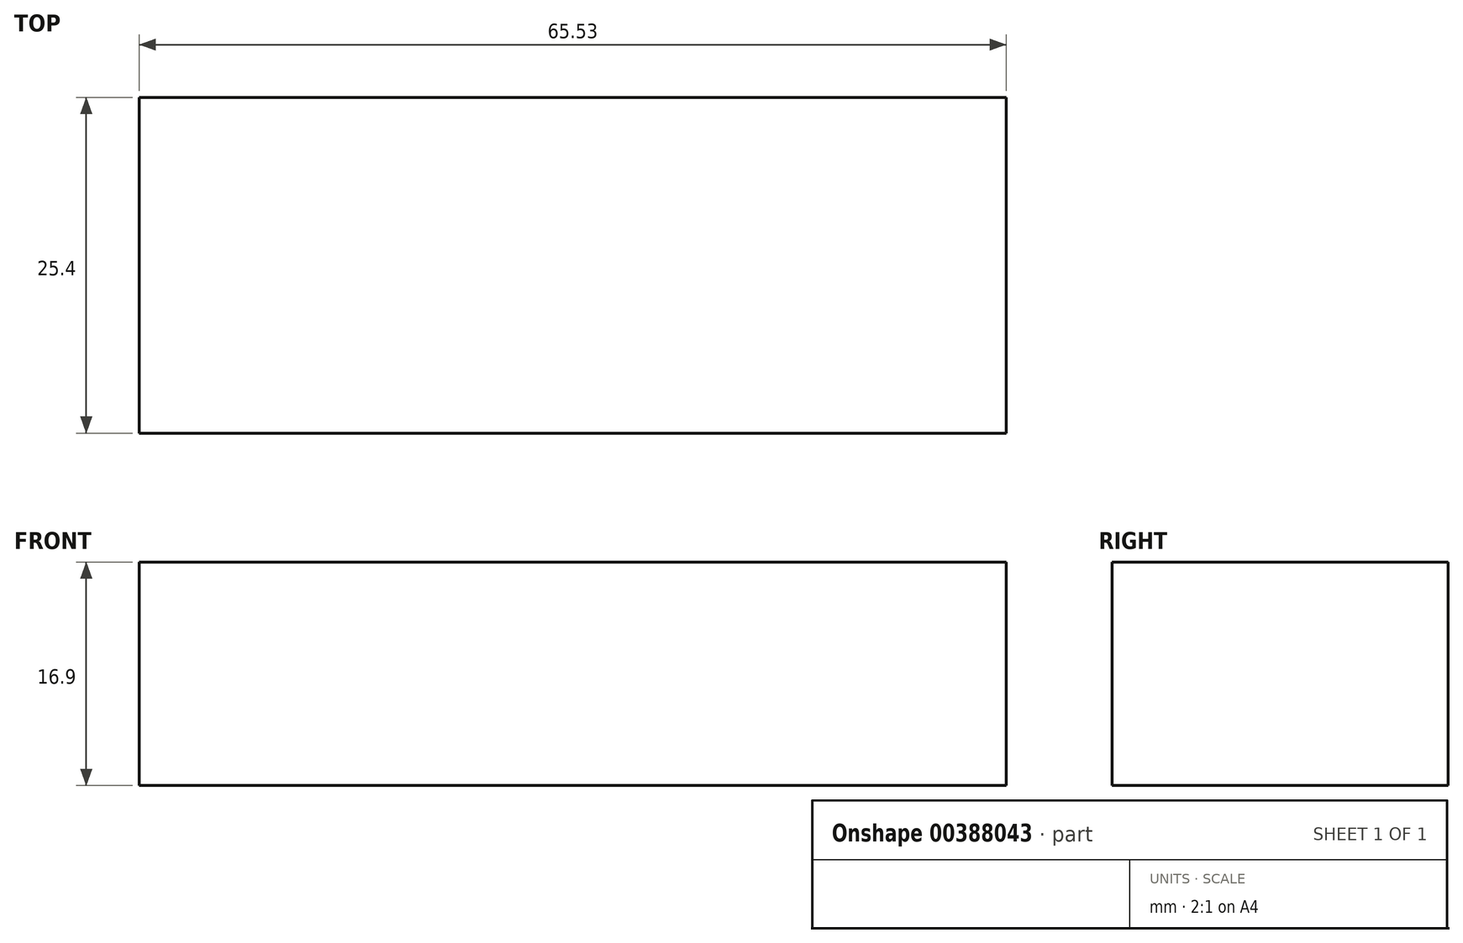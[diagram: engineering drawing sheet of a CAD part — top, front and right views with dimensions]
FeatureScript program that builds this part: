
annotation { "Feature Type Name" : "Feature", "Feature Type Description" : "" }
export const myFeature = defineFeature(function(context is Context, id is Id, definition is map)
    precondition{}
    {
        {
            var Q0;
            Q0=qCreatedBy(makeId("Front.planeOp"),FACE);
            var sketch = newSketch(context, id + "F0", { "sketchPlane" : qUnion([Q0])});
            skLineSegment(sketch, "E0.bottom", {"start": v(0, 0) * mm, "end": v(65.53, 0) * mm});
            skLineSegment(sketch, "E0.top", {"start": v(0, -16.9) * mm, "end": v(65.53, -16.9) * mm});
            skLineSegment(sketch, "E0.left", {"start": v(0, 0) * mm, "end": v(0, -16.9) * mm});
            skLineSegment(sketch, "E0.right", {"start": v(65.53, 0) * mm, "end": v(65.53, -16.9) * mm});
            skSolve(sketch);
        }
        {
            var Q0;
            Q0 = qSketchRegion(id + "F0", true);
            extrude(context, id + "F1", {"entities" : qUnion([Q0]), "depth" : 25.4 * mm});
        }
    });
